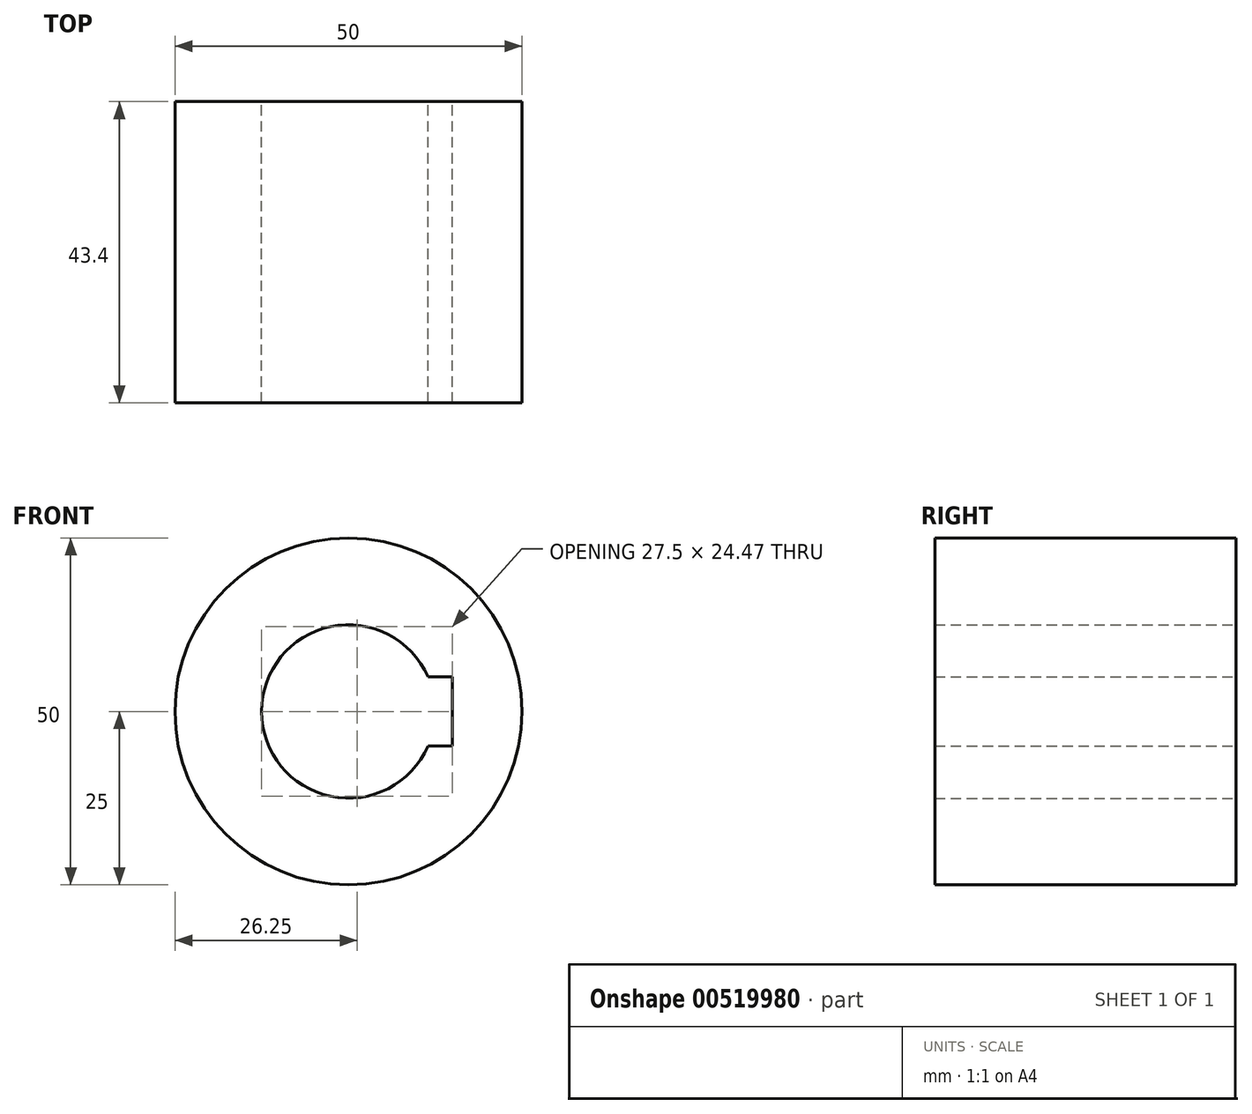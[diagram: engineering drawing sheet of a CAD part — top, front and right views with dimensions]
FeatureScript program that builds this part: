
annotation { "Feature Type Name" : "Feature", "Feature Type Description" : "" }
export const myFeature = defineFeature(function(context is Context, id is Id, definition is map)
    precondition{}
    {
        {
            var Q0;
            Q0=qCreatedBy(makeId("Front.planeOp"),FACE);
            var sketch = newSketch(context, id + "F0", { "sketchPlane" : qUnion([Q0])});
            skCircle(sketch, "E0", {"center": v(0, 0) * mm, "radius": 25 * mm});
            skCircle(sketch, "E1", {"center": v(0, 0) * mm, "radius": 12.5 * mm});
            skLineSegment(sketch, "E2.bottom", {"start": v(-15, 5) * mm, "end": v(15, 5) * mm});
            skLineSegment(sketch, "E2.top", {"start": v(-15, -5) * mm, "end": v(15, -5) * mm});
            skLineSegment(sketch, "E2.left", {"start": v(-15, 5) * mm, "end": v(-15, -5) * mm});
            skLineSegment(sketch, "E2.right", {"start": v(15, 5) * mm, "end": v(15, -5) * mm});
            skSolve(sketch);
        }
        {
            var Q0;
            {var subQ5=sQuery(id+"F0.wireOp",EDGE,"E2.left");Q0=makeQuery(id+"F0.imprint","IMPRINT",FACE,{"disambiguationData":[TD([[makeQuery(id+"F0.imprint","IMPRINT",EDGE,{"derivedFrom":subQ5}),1.0]])]});}
            var Q1;
            Q1=makeQuery(id+"F0.imprint","IMPRINT",FACE,{"disambiguationData":[TD([[makeQuery(id+"F0.imprint","IMPRINT",EDGE,{"derivedFrom":sQuery(id+"F0.wireOp",EDGE,"E0")}),1.0]])]});
            extrude(context, id + "F1", {"entities" : qUnion([Q0, Q1]), "depth" : 43.4 * mm, "offsetDistance" : 25 * mm});
        }
    });
